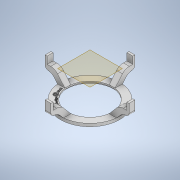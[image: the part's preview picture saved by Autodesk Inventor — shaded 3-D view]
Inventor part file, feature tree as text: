
AUTODESK INVENTOR PART (.ipt)
format: ipt  version: 2022 (Build 260153000, 153)  size: 621,056 bytes
history: native  units: in
note: dims shown in document units (in); Inventor stores cm internally (conversion verified against a paired STEP export)
features: extrude x4, sketch x4, plane x3, emboss x1, pattern_circular x1
ambient origin geometry x8: Origin, YZ Plane, XZ Plane, XY Plane, X Axis, Y Axis, Z Axis, Center Point
bodies: Solid1 (feature_tree)
feature tree (13):
  extrude  "Extrusion1"  Depth=0.3937in
  plane  "Work Plane2"
  extrude  "Extrusion3"  Depth=0.1969in
  plane  "Work Plane3"
  emboss  "Emboss1"
  extrude  "Extrusion4"  Depth=0.0787in TaperAngle=0.0deg
  pattern_circular  "Circular Pattern2"  Count=2  [1 undecoded]
  plane  "Work Plane4"
  extrude  "Extrusion5"  Depth=2.5984in
  sketch  "Sketch1"  dims[d0=0.3937in d1=3.1516in]
  sketch  "Sketch4"  dims[d2=0.1969in d3=0.0in d10=2.9528in]
  sketch  "Sketch6"  dims[d11=3.1575in d12=0.0787in d13=0.0in]
  sketch  "Sketch7"  dims[d17=0.0394in d18=0.0in d27=0.7874in d28=2.5984in d29=0.1969in d31=0.4724in d32=0.7874in d35=0.3937in d36=0.0in d37=0.315in d39=0.5906in d40=0.5906in d41=0.0787in d42=1.5748in d43=360.0deg d45=0.0in d46=0.1969in d47=0.7874in d48=5.315in d49=0.0in d50=0.0in]
note: 1 required parameter value undecoded (feature->parameter linkage not recoverable at this tier; creation-order binding heuristic only, values carry confidence <= 0.55)
